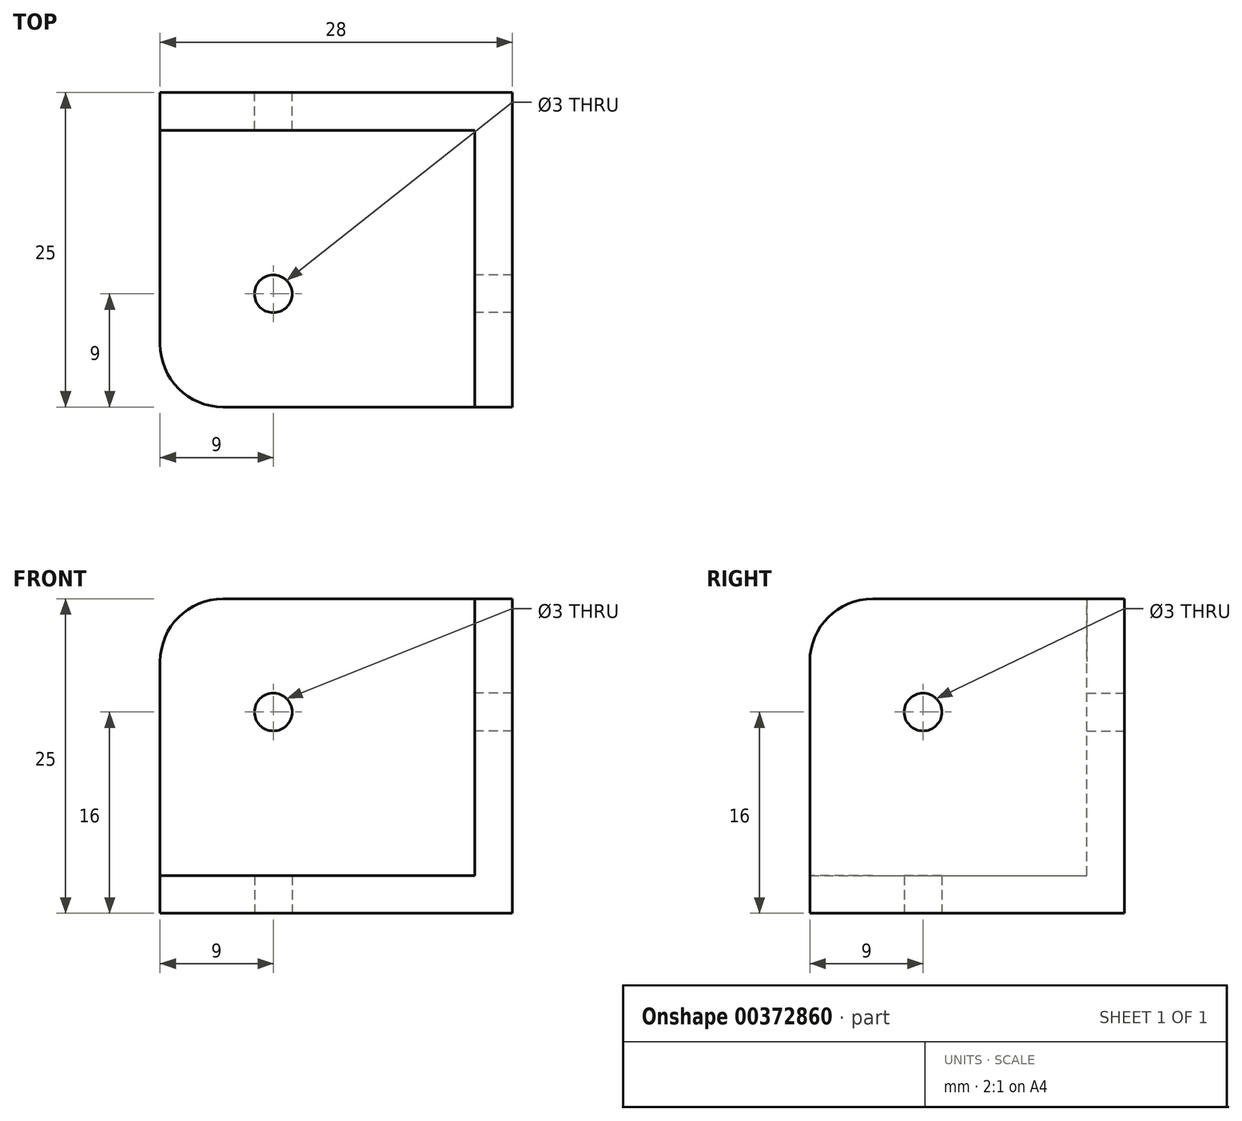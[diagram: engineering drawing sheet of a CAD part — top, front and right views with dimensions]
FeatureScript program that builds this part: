
annotation { "Feature Type Name" : "Feature", "Feature Type Description" : "" }
export const myFeature = defineFeature(function(context is Context, id is Id, definition is map)
    precondition{}
    {
        {
            var Q0;
            Q0=qCreatedBy(makeId("Top.planeOp"),FACE);
            var sketch = newSketch(context, id + "F0", { "sketchPlane" : qUnion([Q0])});
            skLineSegment(sketch, "E0.bottom", {"start": v(0, -25) * mm, "end": v(-25, -25) * mm});
            skLineSegment(sketch, "E0.top", {"start": v(0, 0) * mm, "end": v(-25, 0) * mm});
            skLineSegment(sketch, "E0.left", {"start": v(0, -25) * mm, "end": v(0, 0) * mm});
            skLineSegment(sketch, "E0.right", {"start": v(-25, -25) * mm, "end": v(-25, 0) * mm});
            skCircle(sketch, "E1", {"center": v(-16, -16) * mm, "radius": 1.5 * mm});
            skSolve(sketch);
        }
        {
            var Q0;
            Q0=qCreatedBy(makeId("Right.planeOp"),FACE);
            var sketch = newSketch(context, id + "F1", { "sketchPlane" : qUnion([Q0])});
            skLineSegment(sketch, "E2.bottom", {"start": v(-25, 0) * mm, "end": v(0, 0) * mm});
            skLineSegment(sketch, "E2.top", {"start": v(-25, 25) * mm, "end": v(0, 25) * mm});
            skLineSegment(sketch, "E2.left", {"start": v(-25, 0) * mm, "end": v(-25, 25) * mm});
            skLineSegment(sketch, "E2.right", {"start": v(0, 0) * mm, "end": v(0, 25) * mm});
            skCircle(sketch, "E3", {"center": v(-16, 16) * mm, "radius": 1.5 * mm});
            skSolve(sketch);
        }
        {
            var Q0;
            Q0=qCreatedBy(makeId("Front.planeOp"),FACE);
            var sketch = newSketch(context, id + "F2", { "sketchPlane" : qUnion([Q0])});
            skLineSegment(sketch, "E4.bottom", {"start": v(-25, 0) * mm, "end": v(0, 0) * mm});
            skLineSegment(sketch, "E4.top", {"start": v(-25, 25) * mm, "end": v(0, 25) * mm});
            skLineSegment(sketch, "E4.left", {"start": v(-25, 0) * mm, "end": v(-25, 25) * mm});
            skLineSegment(sketch, "E4.right", {"start": v(0, 0) * mm, "end": v(0, 25) * mm});
            skCircle(sketch, "E5", {"center": v(-16, 16) * mm, "radius": 1.5 * mm});
            skSolve(sketch);
        }
        {
            var Q0;
            Q0 = qSketchRegion(id + "F0", true);
            extrude(context, id + "F3", {"entities" : qUnion([Q0]), "depth" : 3 * mm});
        }
        {
            var Q0;
            Q0=makeQuery(id+"F3.opExtrude","SWEPT_EDGE",EDGE,{"disambiguationData":[OSD([sQuery(id+"F0.wireOp",EDGE,"E0.bottom"),sQuery(id+"F0.wireOp",EDGE,"E0.right")])]});
            fillet(context, id + "F4", {"entities" : qUnion([Q0]), "radius" : 5 * mm, "allowEdgeOverflow" : false});
        }
        {
            var Q0;
            Q0=makeQuery(id+"F1.imprint","IMPRINT",FACE,{"disambiguationData":[TD([[makeQuery(id+"F1.imprint","IMPRINT",EDGE,{"derivedFrom":sQuery(id+"F1.wireOp",EDGE,"E2.bottom")}),1.0]])]});
            extrude(context, id + "F5", {"entities" : qUnion([Q0]), "operationType" : NewBodyOperationType.ADD, "depth" : 3 * mm});
        }
        {
            var Q0;
            Q0=makeQuery(id+"F5.opExtrude","SWEPT_EDGE",EDGE,{"disambiguationData":[OSD([sQuery(id+"F1.wireOp",EDGE,"E2.top"),sQuery(id+"F1.wireOp",EDGE,"E2.left")])]});
            fillet(context, id + "F6", {"entities" : qUnion([Q0]), "radius" : 5 * mm, "tangentPropagation" : true, "allowEdgeOverflow" : false});
        }
        {
            var Q0;
            Q0=makeQuery(id+"F2.imprint","IMPRINT",FACE,{"disambiguationData":[TD([[makeQuery(id+"F2.imprint","IMPRINT",EDGE,{"derivedFrom":sQuery(id+"F2.wireOp",EDGE,"E4.bottom")}),1.0]])]});
            extrude(context, id + "F7", {"entities" : qUnion([Q0]), "operationType" : NewBodyOperationType.ADD, "depth" : 3 * mm});
        }
        {
            var Q0;
            Q0=makeQuery(id+"F7.opExtrude","SWEPT_EDGE",EDGE,{"disambiguationData":[OSD([sQuery(id+"F2.wireOp",EDGE,"E4.top"),sQuery(id+"F2.wireOp",EDGE,"E4.left")])]});
            fillet(context, id + "F8", {"entities" : qUnion([Q0]), "radius" : 5 * mm, "tangentPropagation" : true, "allowEdgeOverflow" : false});
        }
    });
